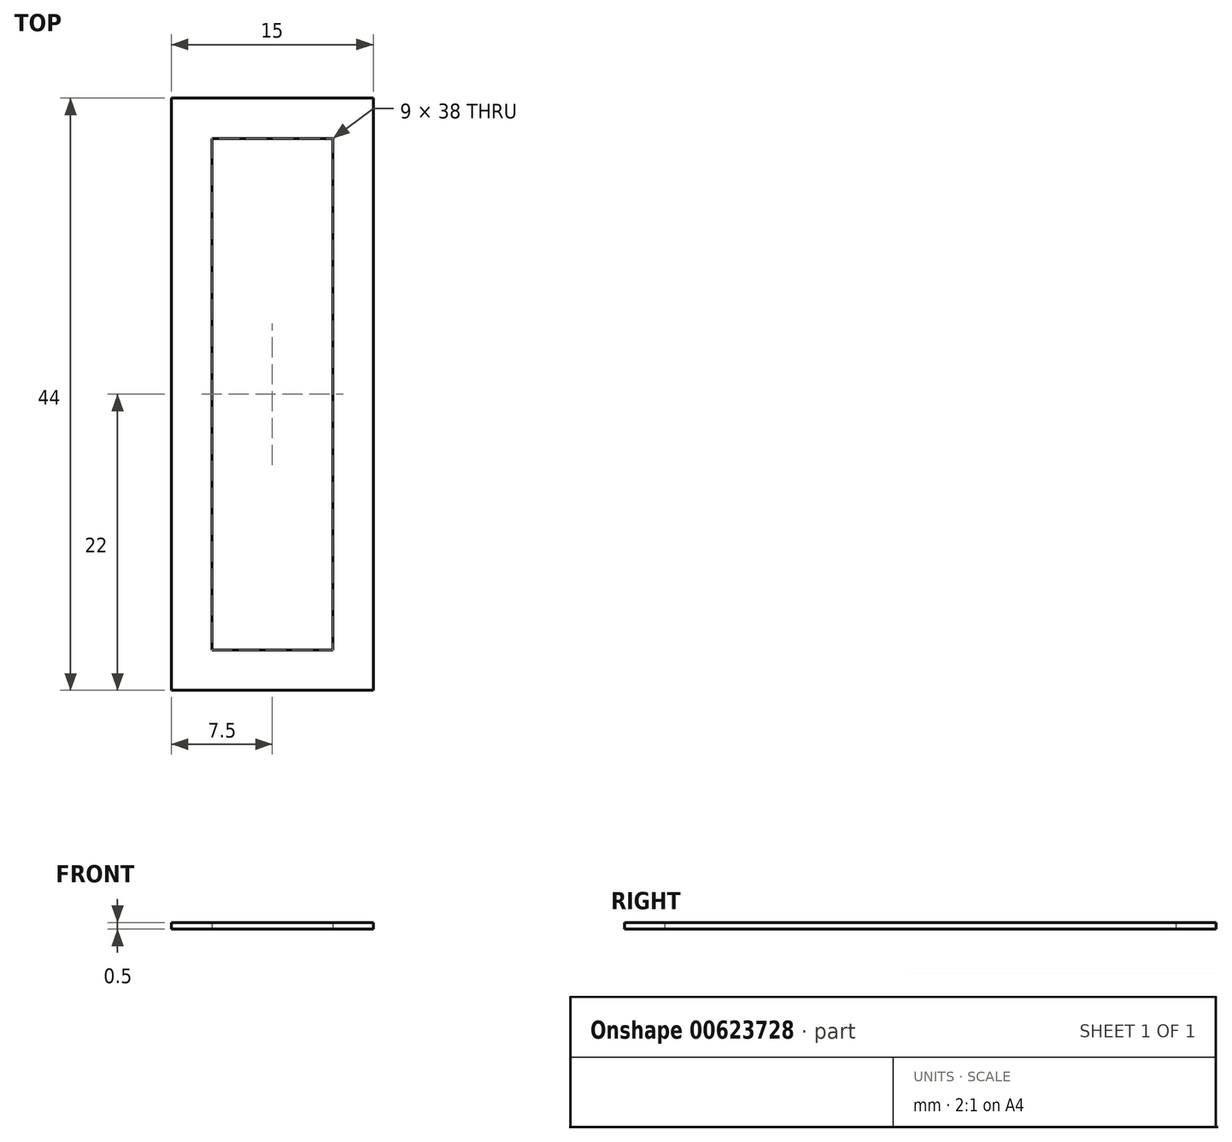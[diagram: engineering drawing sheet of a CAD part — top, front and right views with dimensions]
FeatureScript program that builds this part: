
annotation { "Feature Type Name" : "Feature", "Feature Type Description" : "" }
export const myFeature = defineFeature(function(context is Context, id is Id, definition is map)
    precondition{}
    {
        {
            var Q0;
            Q0=qCreatedBy(makeId("Top.planeOp"),FACE);
            var sketch = newSketch(context, id + "F0", { "sketchPlane" : qUnion([Q0])});
            skLineSegment(sketch, "E0.bottom", {"start": v(7.5, 22) * mm, "end": v(-7.5, 22) * mm});
            skLineSegment(sketch, "E0.top", {"start": v(7.5, -22) * mm, "end": v(-7.5, -22) * mm});
            skLineSegment(sketch, "E0.left", {"start": v(7.5, 22) * mm, "end": v(7.5, -22) * mm});
            skLineSegment(sketch, "E0.right", {"start": v(-7.5, 22) * mm, "end": v(-7.5, -22) * mm});
            skPoint(sketch, "E0.middle", {"position": v(0, 0) * mm});
            skLineSegment(sketch, "E1.bottom", {"start": v(4.5, 19) * mm, "end": v(-4.5, 19) * mm});
            skLineSegment(sketch, "E1.top", {"start": v(4.5, -19) * mm, "end": v(-4.5, -19) * mm});
            skLineSegment(sketch, "E1.left", {"start": v(4.5, 19) * mm, "end": v(4.5, -19) * mm});
            skLineSegment(sketch, "E1.right", {"start": v(-4.5, 19) * mm, "end": v(-4.5, -19) * mm});
            skSolve(sketch);
        }
        {
            var Q0;
            Q0=makeQuery(id+"F0.imprint","IMPRINT",FACE,{"disambiguationData":[TD([[makeQuery(id+"F0.imprint","IMPRINT",EDGE,{"derivedFrom":sQuery(id+"F0.wireOp",EDGE,"E1.bottom")}),1.0]])]});
            var Q1;
            Q1=makeQuery(id+"F0.imprint","IMPRINT",FACE,{"disambiguationData":[TD([[makeQuery(id+"F0.imprint","IMPRINT",EDGE,{"derivedFrom":sQuery(id+"F0.wireOp",EDGE,"E0.bottom")}),1.0]])]});
            extrude(context, id + "F1", {"entities" : qUnion([Q0, Q1]), "depth" : 0.5 * mm, "offsetDistance" : 25 * mm});
        }
        {
            var Q0;
            Q0=makeQuery(id+"F0.imprint","IMPRINT",FACE,{"disambiguationData":[TD([[makeQuery(id+"F0.imprint","IMPRINT",EDGE,{"derivedFrom":sQuery(id+"F0.wireOp",EDGE,"E1.bottom")}),1.0]])]});
            extrude(context, id + "F2", {"entities" : qUnion([Q0]), "operationType" : NewBodyOperationType.REMOVE, "depth" : 25 * mm, "offsetDistance" : 25 * mm});
        }
    });
